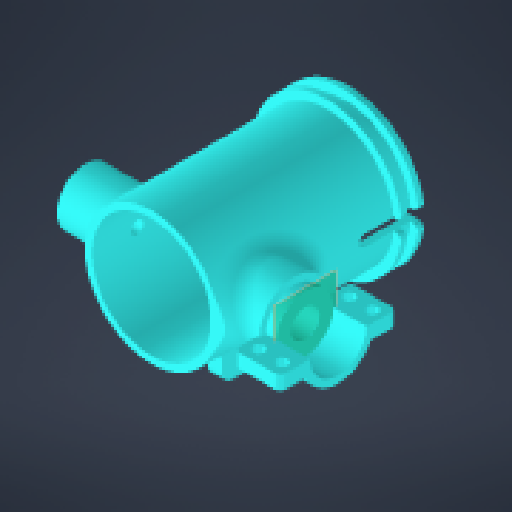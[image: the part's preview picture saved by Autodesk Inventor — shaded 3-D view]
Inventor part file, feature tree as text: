
AUTODESK INVENTOR PART (.ipt)
format: ipt  version: 2024 (Build 280153000, 153)  size: 613,888 bytes
history: native  units: mm
features: sketch x15, extrude x13, other x12, fillet x7, revolve x2, mirror x1, reference x1
ambient origin geometry x8: Origin, YZ Plane, XZ Plane, XY Plane, X Axis, Y Axis, Z Axis, Center Point
bodies: Body1 (feature_tree)
feature tree (51):
  other  "Твердое тело1"
  extrude  "Выдавливание1"  Depth=70.0mm
  other  "РабПлоскость2"
  revolve  "Вращение1"
  fillet  "Сопряжение1"  [1 undecoded]
  extrude  "Выдавливание2"  Depth=42.0mm
  extrude  "Выдавливание3"  Depth=47.0mm
  extrude  "Выдавливание4"  [1 undecoded]
  fillet  "Сопряжение2"  [1 undecoded]
  extrude  "Выдавливание5"  Depth=10.0mm
  revolve  "Вращение2"
  fillet  "Сопряжение3"  Radius=20.0mm
  extrude  "Выдавливание6"  Depth=36.0mm
  fillet  "Сопряжение4"  [1 undecoded]
  fillet  "Сопряжение5"  Radius=12.0mm
  extrude  "Выдавливание8"  Depth=5.0mm
  extrude  "Выдавливание11"  Depth=7.5mm
  extrude  "Выдавливание12"  Depth=40.0mm
  fillet  "Сопряжение6"  [1 undecoded]
  mirror  "Зеркальное отражение5"
  other  "РабПлоскость7"
  extrude  "Выдавливание14"  Depth=3.0mm
  extrude  "Выдавливание15"  Depth=5.0mm
  fillet  "Сопряжение7"  Radius=8.0mm
  extrude  "Выдавливание16"  TaperAngle=0.0deg  [1 undecoded]
  other  "РабПлоскость8"
  extrude  "Выдавливание17"  TaperAngle=0.0deg  [1 undecoded]
  sketch  "Эскиз1"
  reference  "Ссылка1"
  sketch  "Эскиз3"
  sketch  "Эскиз4"
  sketch  "Эскиз5"
  sketch  "Эскиз6"
  sketch  "Эскиз7"
  sketch  "Эскиз8"
  sketch  "Эскиз9"
  sketch  "Эскиз11"
  sketch  "Эскиз14"
  sketch  "Эскиз15"
  other  "РабПлоскость6"
  sketch  "Эскиз17"
  sketch  "Эскиз18"
  sketch  "Эскиз19"
  sketch  "Эскиз21"
  parser-record x2  (decoder bookkeeping rows leaked as tree rows — omitted from the tree; the rows remain in map.json)
  other  "motor_assembly_M.iam"
  other  "motor:1"
  other  "rigt_motor_asembly.iam"
  other  "bushing_assembly:2"
  other  "bushing:1"
note: 7 required parameter values undecoded (feature->parameter linkage not recoverable at this tier; creation-order binding heuristic only, values carry confidence <= 0.55)
note: 2 file-system paths scrubbed to <path> (originals preserved in map.json)
